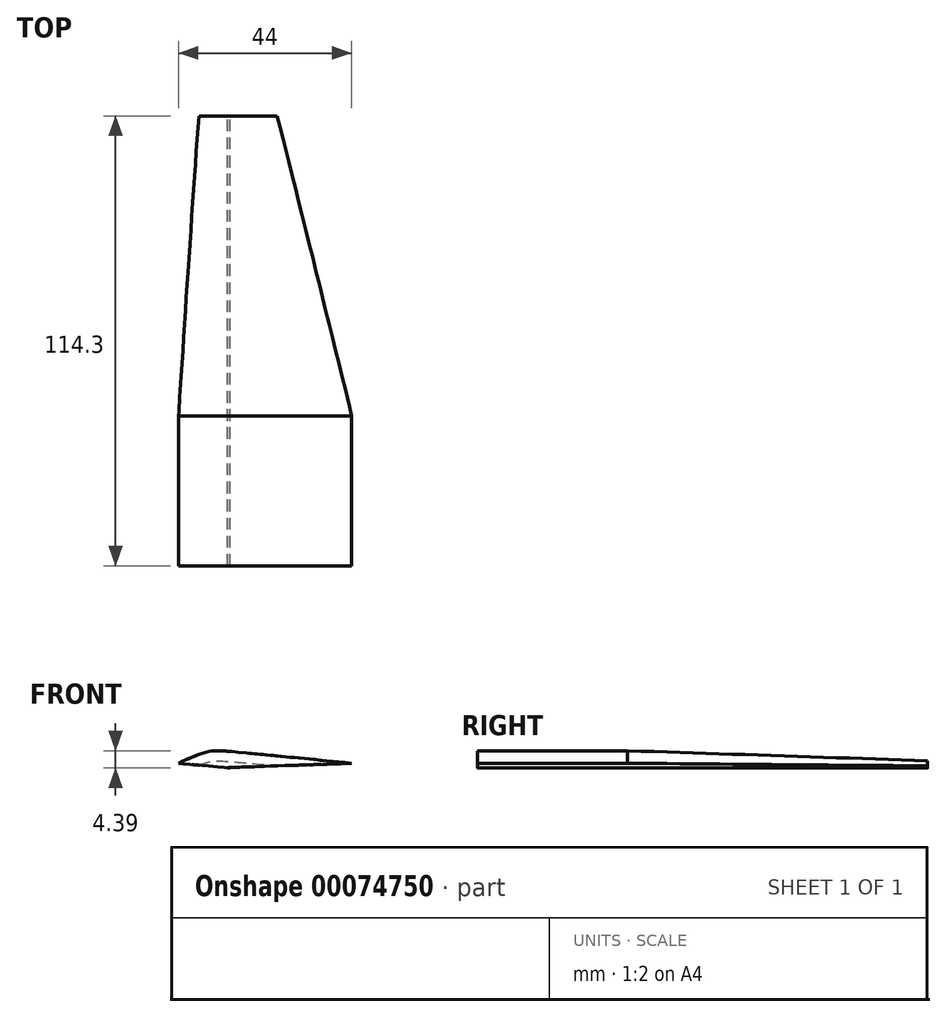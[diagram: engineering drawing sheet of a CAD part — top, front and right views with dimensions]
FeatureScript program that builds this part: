
annotation { "Feature Type Name" : "Feature", "Feature Type Description" : "" }
export const myFeature = defineFeature(function(context is Context, id is Id, definition is map)
    precondition{}
    {
        {
            var Q0;
            Q0=qCreatedBy(makeId("Front.planeOp"),FACE);
            var sketch = newSketch(context, id + "F0", { "sketchPlane" : qUnion([Q0])});
            skFitSpline(sketch, "E0", {"points": [v(0, 0) * mm, v(9.34, 3.16) * mm, v(44, 0) * mm], "startDerivative": vector(57.24, 27.5) * mm, "endDerivative": vector(159.32, -15.88) * mm});
            skFitSpline(sketch, "E1", {"points": [v(44, 0) * mm, v(12.72, -1.17) * mm, v(0, 0) * mm], "startDerivative": vector(-156.59, -5.73) * mm, "endDerivative": vector(-112.58, 10.71) * mm});
            skSolve(sketch);
        }
        {
            var Q0;
            Q0 = qSketchRegion(id + "F0", true);
            extrude(context, id + "F1", {"entities" : qUnion([Q0]), "oppositeDirection" : true, "depth" : 114.3 * mm});
        }
        {
            var Q0;
            Q0=makeQuery(id+"F1.opExtrude","CAP_EDGE",EDGE,{"disambiguationData":[OSD([sQuery(id+"F0.wireOp",EDGE,"E0")])],"isStart":false});
            chamfer(context, id + "F2", {"entities" : qUnion([Q0]), "chamferType" : ChamferType.TWO_OFFSETS, "width1" : 2.54 * mm, "oppositeDirection" : false, "width2" : 76.2 * mm, "tangentPropagation" : true});
        }
    });
